# Revit family: Plumbing_Joints_Aignep_Threaded-Clamp-Hanger-90860
name_source: partatom
category: Pipe Accessories
revit_build: Autodesk Revit 2018 (Build: 20190510_1515(x64)
units: mm (PartAtom-declared; Revit-internal decimal feet)

## family parameters
Cut with Voids When Loaded = No
Host = Face
OmniClass Number = 23.27.43.00
OmniClass Title = Pipe Fittings
Part Type = Normal
Round Connector Dimension = Use Diameter
Shared = No

## types (1)
- 90861
    Article Code = 90861 00 001
    Assembly Code = D2040100
    BIMobject category = Joints
    Default Elevation = 1219 mm
    Description = Threaded clamp hanger
    Design country = Italy
    Edition number = 1
    IFC Classification = Pipe Fitting
    K = 18 mm
    Keynote = 15400
    M = 8 mm  [stored 0.0262467 ft]
    Manufacturer = Aignep Spa
    Manufacturer country = Italy
    Manufacturer name = Aignep Spa
    Material main = Steel
    Model = 90861
    OmniClass Code = 23-27 43 00
    OmniClass Description = Pipe Fittings
    Product Guid = 5afffd7f-b1a5-446c-9dcc-7c3c883e4ecb
    Product Material = AIGNEP - Steel - Brushed
    Product SKU = Threaded-Clamp-Hanger-90861
    Product certification = https://www.aignep.com
    Product data url = https://www.bimobject.com
    Product family = INFINITY
    Product group = Fittings
    Product name = Threaded Clamp Hanger - 90861
    Product url = https://www.aignep.com
    QR code = https://www.bimobject.com
    URL = https://www.aignep.com

note: [stored X ft] marks values corroborated as IEEE doubles in the binary element streams (Revit-internal decimal feet)

## geometry (parser evidence)
native form markers: Sweep x2
no freeform markers — native parametric forms only
